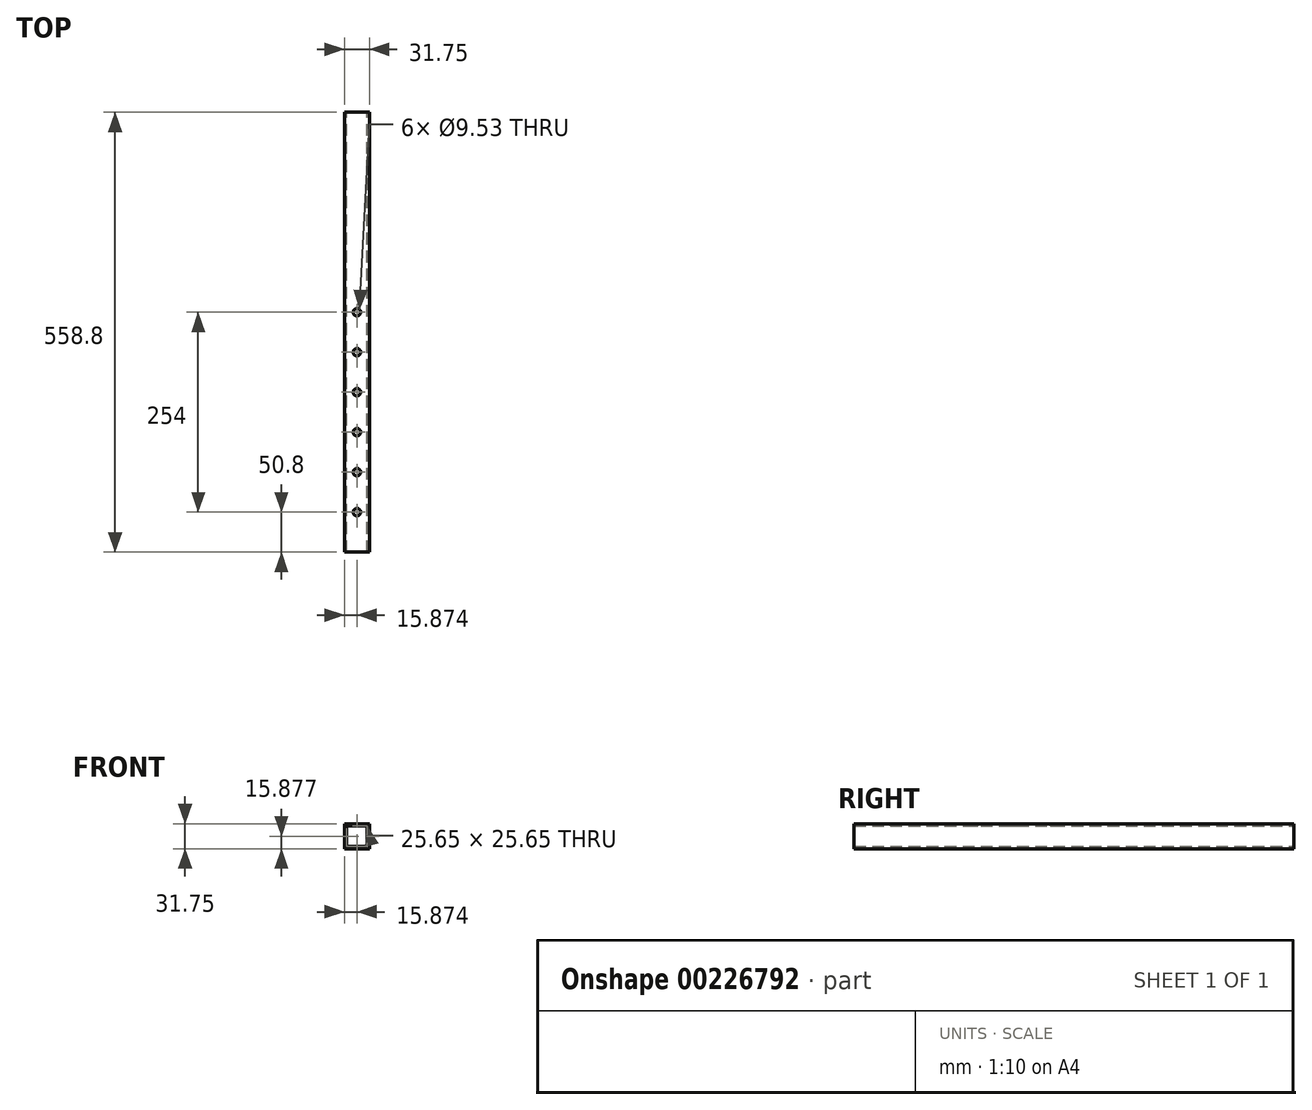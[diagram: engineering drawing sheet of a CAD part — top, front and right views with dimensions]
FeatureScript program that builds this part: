
annotation { "Feature Type Name" : "Feature", "Feature Type Description" : "" }
export const myFeature = defineFeature(function(context is Context, id is Id, definition is map)
    precondition{}
    {
        {
            var Q0;
            Q0=qCreatedBy(makeId("Front.planeOp"),FACE);
            var sketch = newSketch(context, id + "F0", { "sketchPlane" : qUnion([Q0])});
            skLineSegment(sketch, "E0.bottom", {"start": v(-57.25, 47.66) * mm, "end": v(-25.5, 47.66) * mm});
            skLineSegment(sketch, "E0.top", {"start": v(-57.25, 15.91) * mm, "end": v(-25.5, 15.91) * mm});
            skLineSegment(sketch, "E0.left", {"start": v(-57.25, 47.66) * mm, "end": v(-57.25, 15.91) * mm});
            skLineSegment(sketch, "E0.right", {"start": v(-25.5, 47.66) * mm, "end": v(-25.5, 15.91) * mm});
            skPoint(sketch, "E1", {"position": v(-54.2, 47.66) * mm});
            skPoint(sketch, "E2", {"position": v(-57.25, 44.61) * mm});
            skPoint(sketch, "E3", {"position": v(-54.2, 44.61) * mm});
            skLineSegment(sketch, "E4.bottom", {"start": v(-54.2, 44.61) * mm, "end": v(-28.55, 44.61) * mm});
            skLineSegment(sketch, "E4.top", {"start": v(-54.2, 18.96) * mm, "end": v(-28.55, 18.96) * mm});
            skLineSegment(sketch, "E4.left", {"start": v(-54.2, 44.61) * mm, "end": v(-54.2, 18.96) * mm});
            skLineSegment(sketch, "E4.right", {"start": v(-28.55, 44.61) * mm, "end": v(-28.55, 18.96) * mm});
            skSolve(sketch);
        }
        {
            var Q0;
            Q0=makeQuery(id+"F0.imprint","IMPRINT",FACE,{"disambiguationData":[TD([[makeQuery(id+"F0.imprint","IMPRINT",EDGE,{"derivedFrom":sQuery(id+"F0.wireOp",EDGE,"E0.bottom")}),-1.0]])]});
            extrude(context, id + "F1", {"entities" : qUnion([Q0]), "depth" : 558.8 * mm});
        }
        {
            var Q0;
            Q0=makeQuery(id+"F1.opExtrude","SWEPT_FACE",FACE,{"disambiguationData":[OSD([sQuery(id+"F0.wireOp",EDGE,"E0.bottom")])]});
            var sketch = newSketch(context, id + "F2", { "sketchPlane" : qUnion([Q0])});
            skPoint(sketch, "E5", {"position": v(-41.38, -508) * mm});
            skPoint(sketch, "E5.positionSnap0", {"position": v(-41.38, -558.8) * mm});
            skPoint(sketch, "E6", {"position": v(-41.38, -457.2) * mm});
            skPoint(sketch, "E7", {"position": v(-41.38, -406.4) * mm});
            skPoint(sketch, "E8", {"position": v(-41.38, -355.6) * mm});
            skPoint(sketch, "E9", {"position": v(-41.38, -304.8) * mm});
            skPoint(sketch, "E10", {"position": v(-41.38, -254) * mm});
            skSolve(sketch);
        }
        {
            var Q0;
            Q0=sQuery(id+"F2.wireOp",VERTEX,"E5");
            var Q1;
            Q1=sQuery(id+"F2.wireOp",VERTEX,"E6");
            var Q2;
            Q2=sQuery(id+"F2.wireOp",VERTEX,"E7");
            var Q3;
            Q3=sQuery(id+"F2.wireOp",VERTEX,"E8");
            var Q4;
            Q4=sQuery(id+"F2.wireOp",VERTEX,"E9");
            var Q5;
            Q5=sQuery(id+"F2.wireOp",VERTEX,"E10");
            var Q6;
            Q6=makeQuery(id+"F1.opExtrude","SWEPT_BODY",BODY,{"disambiguationData":[OSD([sQuery(id+"F0.wireOp",EDGE,"E0.bottom"),sQuery(id+"F0.wireOp",EDGE,"E0.top"),sQuery(id+"F0.wireOp",EDGE,"E0.left"),sQuery(id+"F0.wireOp",EDGE,"E0.right"),sQuery(id+"F0.wireOp",EDGE,"E4.bottom"),sQuery(id+"F0.wireOp",EDGE,"E4.top"),sQuery(id+"F0.wireOp",EDGE,"E4.left"),sQuery(id+"F0.wireOp",EDGE,"E4.right")])]});
            hole(context, id + "F3", {"style" : HoleStyle.SIMPLE, "endStyle" : HoleEndStyle.BLIND, "holeDiameter" : 9.52 * mm, "holeDepth" : 12.7 * mm, "locations" : qUnion([Q0, Q1, Q2, Q3, Q4, Q5]), "scope" : qUnion([Q6])});
        }
    });
